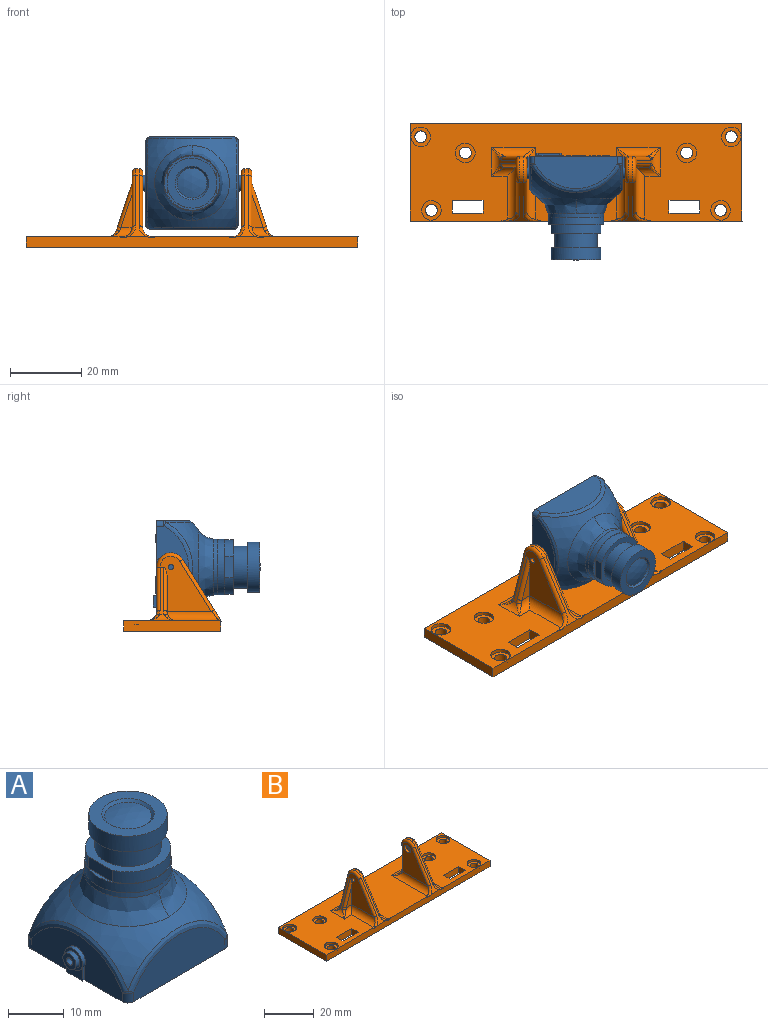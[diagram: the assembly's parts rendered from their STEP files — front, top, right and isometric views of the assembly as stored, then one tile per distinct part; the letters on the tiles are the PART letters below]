
ASSEMBLY  parts=2 mates=1
PART A: 309 faces, bbox 33.6x27.9x30.4 mm
  f0: sphere r=14.51mm, area 0mm2, adj f1
  f1: cone r=4.2mm half-angle=44deg, axis (0,0,1), area 19.4mm2, adj f0,f2
  f2: plane 14.21x14.21mm, normal (0,0,1), area 84.8mm2, adj f1,f3
  f3: cylinder r=7mm len=14mm, axis (0,0,-1), area 149.5mm2, adj f2,f4
  f4: plane 14.17x14.17mm, normal (0,0,-1), area 44.8mm2, adj f3,f5
  f5: cylinder r=5.9mm len=11.8mm, axis (0,0,-1), area 148.3mm2, adj f4,f6
  f6: plane 15.49x14.29mm, normal (0,0,1), area 67.2mm2, adj f5,f8,f9,f10,f11
  f7: plane 1.52x1.52mm, normal (-1,0,0), area 1.8mm2, adj f14
  f8: plane 5.92x2.5mm, normal (1,0,0), area 14.8mm2, adj f6,f9,f11,f13
  f9: cylinder r=7.6mm len=14mm, axis (0,0,1), area 44.5mm2, adj f6,f8,f10,f13
  f10: plane 5.92x2.5mm, normal (-1,0,0), area 14.8mm2, adj f6,f9,f11,f13
  f11: cylinder r=7.6mm len=14mm, axis (0,0,1), area 44.5mm2, adj f6,f8,f10,f13
  f12: plane 1.52x1.52mm, normal (1,0,0), area 1.8mm2, adj f16
  f13: plane 15.73x15.73mm, normal (0,0,1), area 11.8mm2, adj f8,f9,f10,f11,f15
  f14: cylinder r=0.75mm len=1.8mm, axis (1,0,0), area 8.5mm2, adj f7,f17
  f15: cylinder r=7.75mm len=15.5mm, axis (0,0,-1), area 97.4mm2, adj f13,f18
  f16: cylinder r=0.75mm len=1.8mm, axis (-1,0,0), area 8.5mm2, adj f12,f19
  f17: plane 3.35x3.35mm, normal (-1,0,0), area 6.8mm2, adj f14,f20
  f18: cone r=7.75mm half-angle=5.4deg, axis (0,0,-1), area 47.3mm2, adj f15,f21,f22
  f19: plane 3.35x3.35mm, normal (1,0,0), area 6.8mm2, adj f16,f23
  f20: cylinder r=1.65mm len=3.3mm, axis (1,0,0), area 10.4mm2, adj f17,f30
  f21: bspline ~20.97x10.73mm, area 147.9mm2, adj f18,f22,f31
  f22: bspline ~20.97x10.73mm, area 147.9mm2, adj f18,f21,f31
  f23: cylinder r=1.65mm len=3.3mm, axis (-1,0,0), area 10.4mm2, adj f19,f32
  f24: plane 0.96x0.69mm, normal (0,0,-1), area 0.3mm2, adj f33,f34,f35,f36,f37
  f25: plane 1.01x0.76mm, normal (0,0,-1), area 0.6mm2, adj f38,f39,f40
  f26: plane 0.99x0.91mm, normal (0,0,-1), area 0.7mm2, adj f41
  f27: plane 0.96x0.77mm, normal (0,0,-1), area 0.6mm2, adj f42,f43,f44,f45
  f28: plane 0.96x0.77mm, normal (0,0,-1), area 0.6mm2, adj f46,f47,f48,f49
  f29: plane 0.96x0.77mm, normal (0,0,-1), area 0.6mm2, adj f50,f51,f52,f53
  f30: plane 4.56x4.56mm, normal (-1,0,0), area 7.3mm2, adj f20,f61
  f31: sphere r=18.88mm, area 390.1mm2, adj f21,f22,f55,f59,f63,f67
  f32: plane 4.56x4.56mm, normal (1,0,0), area 7.3mm2, adj f23,f69
  f33: plane 0.58x0.25mm, normal (0.94,0.35,0), area 0.2mm2, adj f24,f34,f37,f75
  f34: bspline ~0.38x0.25mm, area 0.1mm2, adj f24,f33,f35,f75
  f35: bspline ~0.42x0.25mm, area 0.1mm2, adj f24,f34,f36,f75
  f36: plane 0.55x0.25mm, normal (-0.93,0.36,0), area 0.1mm2, adj f24,f35,f37,f75
  f37: plane 0.69x0.25mm, normal (0,-1,0), area 0.2mm2, adj f24,f33,f36,f75
  f38: plane 0.71x0.25mm, normal (1,0,0), area 0.2mm2, adj f25,f39,f40,f78
  f39: bspline ~0.73x0.25mm, area 0.2mm2, adj f25,f38,f40,f78
  f40: bspline ~0.95x0.69mm, area 0.4mm2, adj f25,f38,f39,f78
  f41: bspline ~0.95x0.89mm, area 0.7mm2, adj f26,f84
  f42: plane 0.9x0.25mm, normal (0,-1,0), area 0.2mm2, adj f27,f43,f44,f86
  f43: bspline ~0.49x0.25mm, area 0.1mm2, adj f27,f42,f45,f86
  f44: bspline ~0.59x0.25mm, area 0.2mm2, adj f27,f42,f45,f86
  f45: bspline ~0.8x0.25mm, area 0.2mm2, adj f27,f43,f44,f86
  f46: plane 0.9x0.25mm, normal (0,-1,0), area 0.2mm2, adj f28,f47,f48,f89
  f47: bspline ~0.49x0.25mm, area 0.1mm2, adj f28,f46,f49,f89
  f48: bspline ~0.59x0.25mm, area 0.2mm2, adj f28,f46,f49,f89
  f49: bspline ~0.8x0.25mm, area 0.2mm2, adj f28,f47,f48,f89
  f50: plane 0.9x0.25mm, normal (0,-1,0), area 0.2mm2, adj f29,f51,f52,f92
  f51: bspline ~0.49x0.25mm, area 0.1mm2, adj f29,f50,f53,f92
  f52: bspline ~0.59x0.25mm, area 0.2mm2, adj f29,f50,f53,f92
  f53: bspline ~0.8x0.25mm, area 0.2mm2, adj f29,f51,f52,f92
  f54: sphere r=1.5mm, area 0.6mm2, adj f55,f67,f98
  f55: bspline ~27.34x11.13mm, area 37.5mm2, adj f31,f54,f56,f99
  f56: sphere r=1.5mm, area 0.6mm2, adj f55,f59,f100
  f57: plane 4.09x3.01mm, normal (-1,0,0), area 8.2mm2, adj f58,f60,f61,f101
  f58: plane 2.92x0.5mm, normal (0,-1,0), area 1.5mm2, adj f57,f61,f101,f102
  f59: bspline ~27.64x11.52mm, area 37.5mm2, adj f31,f56,f62,f102
  f60: plane 2.92x0.5mm, normal (0,1,0), area 1.5mm2, adj f57,f61,f101,f102
  f61: cylinder r=2.25mm len=4.5mm, axis (1,0,0), area 8.8mm2, adj f30,f57,f58,f60,f102
  f62: sphere r=1.5mm, area 0.6mm2, adj f59,f63,f103
  f63: bspline ~27.34x11.12mm, area 37.5mm2, adj f31,f62,f64,f104
  f64: sphere r=1.5mm, area 0.6mm2, adj f63,f67,f105
  f65: plane 4.09x3.01mm, normal (1,0,0), area 8.2mm2, adj f66,f68,f69,f106
  f66: plane 2.92x0.5mm, normal (0,1,0), area 1.5mm2, adj f65,f69,f106,f107
  f67: bspline ~27.64x11.52mm, area 37.5mm2, adj f31,f54,f64,f107
  f68: plane 2.92x0.5mm, normal (0,-1,0), area 1.5mm2, adj f65,f69,f106,f107
  f69: cylinder r=2.25mm len=4.5mm, axis (-1,0,0), area 8.8mm2, adj f32,f65,f66,f68,f107
  f70: plane 6x2.95mm, normal (0,0,-1), area 17.7mm2, adj f108,f302,f303,f304
  f71: plane 5.78x1.83mm, normal (0,0,-1), area 9.7mm2, adj f109,f110,f111,f112
  f72: plane 5.78x1.83mm, normal (0,0,-1), area 9.7mm2, adj f113,f114,f115,f116
  f73: plane 5.78x1.83mm, normal (0,0,-1), area 9.7mm2, adj f117,f118,f119,f120
  f74: plane 2.04x1.97mm, normal (0,0,-1), area 1.9mm2, adj f121,f122,f123,f124,f125,f126,f127,f128
  f75: plane 1.99x1.84mm, normal (0,0,-1), area 1.2mm2, adj f33,f34,f35,f36,f37,f136,f137,f138
  f76: plane 2.09x1.78mm, normal (0,0,-1), area 1.2mm2, adj f144,f145,f146,f147
  f77: plane 1.99x1.84mm, normal (0,0,-1), area 1mm2, adj f148,f149,f150,f151,f152,f153,f154,f155
  f78: plane 2.04x1.53mm, normal (0,0,-1), area 1.2mm2, adj f38,f39,f40,f157,f158,f159,f160,f161
  f79: plane 1.99x1.34mm, normal (0,0,-1), area 1mm2, adj f162,f163,f164,f165,f166,f167,f168,f169
  f80: plane 1.99x0.27mm, normal (0,0,-1), area 0.5mm2, adj f172,f173,f174,f175
  f81: plane 1.99x1.54mm, normal (0,0,-1), area 1.5mm2, adj f176,f177,f178,f179,f180,f181,f182,f183
  f82: plane 1.99x0.27mm, normal (0,0,-1), area 0.5mm2, adj f186,f187,f188,f189
  f83: plane 2.04x1.97mm, normal (0,0,-1), area 1.9mm2, adj f190,f191,f192,f193,f194,f195,f196,f197
  f84: plane 1.26x1.26mm, normal (0,0,-1), area 0.5mm2, adj f41,f205
  f85: plane 1.22x1.02mm, normal (0,0,-1), area 0.5mm2, adj f206,f207,f208,f209,f210,f211,f212,f213
  f86: plane 1.22x1.11mm, normal (0,0,-1), area 0.5mm2, adj f42,f43,f44,f45,f214,f215,f216,f217
  f87: plane 1.2x1.17mm, normal (0,0,-1), area 0.4mm2, adj f218,f219,f220,f221,f222,f223,f224,f225
  f88: plane 1.17x0.17mm, normal (0,0,-1), area 0.2mm2, adj f227,f228,f229,f230
  f89: plane 1.22x1.11mm, normal (0,0,-1), area 0.5mm2, adj f46,f47,f48,f49,f231,f232,f233,f234
  f90: plane 1.26x1.25mm, normal (0,0,-1), area 0.6mm2, adj f235,f236,f237,f238,f239,f240,f241,f242
  f91: plane 1.17x1mm, normal (0,0,-1), area 0.6mm2, adj f244,f245,f246,f247,f248,f249,f250,f251
  f92: plane 1.22x1.11mm, normal (0,0,-1), area 0.5mm2, adj f50,f51,f52,f53,f254,f255,f256,f257
  f93: plane 1.2x0.86mm, normal (0,0,-1), area 0.4mm2, adj f258,f259,f260,f261,f262,f263,f264,f265
  f94: plane 0.49x0.14mm, normal (0,0,-1), area 0.1mm2, adj f268,f269,f270,f271
  f95: plane 1.22x0.89mm, normal (0,0,-1), area 0.4mm2, adj f272,f273,f274,f275,f276,f277,f278,f279
  f96: plane 1.22x0.89mm, normal (0,0,-1), area 0.4mm2, adj f281,f282,f283,f284,f285,f286,f287,f288
  f97: plane 1.2x1.17mm, normal (0,0,-1), area 0.4mm2, adj f290,f291,f292,f293,f294,f295,f296,f297
  f98: cylinder r=1.5mm len=2.04mm, axis (0,0,1), area 4.8mm2, adj f54,f99,f107,f305
  f99: plane 23x8.94mm, normal (0,-1,0), area 160mm2, adj f55,f98,f100,f305
  f100: cylinder r=1.5mm len=2.04mm, axis (0,0,-1), area 4.8mm2, adj f56,f99,f102,f305
  f101: plane 4x0.5mm, normal (0,0,-1), area 2mm2, adj f57,f58,f60,f305
  f102: plane 23.01x8.95mm, normal (-1,0,0), area 135.9mm2, adj f58,f59,f60,f61,f100,f103,f305
  f103: cylinder r=1.5mm len=2.04mm, axis (0,0,-1), area 4.8mm2, adj f62,f102,f104,f305
  f104: plane 23x8.94mm, normal (0,1,0), area 160mm2, adj f63,f103,f105,f305
  f105: cylinder r=1.5mm len=2.04mm, axis (0,0,-1), area 4.8mm2, adj f64,f104,f107,f305
  f106: plane 4x0.5mm, normal (0,0,-1), area 2mm2, adj f65,f66,f68,f305
  f107: plane 23.01x8.95mm, normal (1,0,0), area 135.9mm2, adj f66,f67,f68,f69,f98,f105,f305
  f108: plane 6x2mm, normal (0,1,0), area 12mm2, adj f70,f302,f304,f305
  f109: cylinder r=0.9mm len=2mm, axis (0,0,1), area 5.7mm2, adj f71,f110,f112,f305
  f110: plane 3.95x2mm, normal (0,-1,0), area 7.9mm2, adj f71,f109,f111,f305
  f111: cylinder r=0.9mm len=2mm, axis (0,0,1), area 5.7mm2, adj f71,f110,f112,f305
  f112: plane 3.95x2mm, normal (0,1,0), area 7.9mm2, adj f71,f109,f111,f305
  f113: cylinder r=0.9mm len=2mm, axis (0,0,1), area 5.7mm2, adj f72,f114,f116,f305
  f114: plane 3.95x2mm, normal (0,-1,0), area 7.9mm2, adj f72,f113,f115,f305
  f115: cylinder r=0.9mm len=2mm, axis (0,0,1), area 5.7mm2, adj f72,f114,f116,f305
  f116: plane 3.95x2mm, normal (0,1,0), area 7.9mm2, adj f72,f113,f115,f305
  f117: cylinder r=0.9mm len=2mm, axis (0,0,1), area 5.7mm2, adj f73,f118,f120,f305
  f118: plane 3.95x2mm, normal (0,-1,0), area 7.9mm2, adj f73,f117,f119,f305
  f119: cylinder r=0.9mm len=2mm, axis (0,0,1), area 5.7mm2, adj f73,f118,f120,f305
  f120: plane 3.95x2mm, normal (0,1,0), area 7.9mm2, adj f73,f117,f119,f305
  f121: plane 1.99x0.25mm, normal (-1,0,0), area 0.5mm2, adj f74,f122,f135,f305
  f122: plane 0.4x0.25mm, normal (0,-1,0), area 0.1mm2, adj f74,f121,f124,f305
  f123: bspline ~0.29x0.25mm, area 0.1mm2, adj f74,f124,f126,f305
  f124: plane 1.4x0.47mm, normal (0.95,-0.32,0), area 0.4mm2, adj f74,f122,f123,f305
  f125: plane 1.38x0.49mm, normal (-0.94,-0.34,0), area 0.4mm2, adj f74,f126,f127,f305
  f126: bspline ~0.32x0.25mm, area 0.1mm2, adj f74,f123,f125,f305
  f127: plane 0.35x0.25mm, normal (0,-1,0), area 0.1mm2, adj f74,f125,f128,f305
  f128: plane 1.99x0.25mm, normal (1,0,0), area 0.5mm2, adj f74,f127,f129,f305
  f129: plane 0.27x0.25mm, normal (0,1,0), area 0.1mm2, adj f74,f128,f130,f305
  f130: plane 1.66x0.25mm, normal (-1,0,0), area 0.4mm2, adj f74,f129,f131,f305
  f131: plane 1.66x0.59mm, normal (0.94,0.33,0), area 0.4mm2, adj f74,f130,f132,f305
  f132: plane 0.25x0.23mm, normal (0,1,0), area 0.1mm2, adj f74,f131,f133,f305
  f133: plane 1.69x0.57mm, normal (-0.95,0.32,0), area 0.4mm2, adj f74,f132,f134,f305
  f134: plane 1.69x0.25mm, normal (1,0,0), area 0.4mm2, adj f74,f133,f135,f305
  f135: plane 0.27x0.25mm, normal (0,1,0), area 0.1mm2, adj f74,f121,f134,f305
  f136: plane 1.99x0.76mm, normal (-0.93,-0.36,0), area 0.5mm2, adj f75,f137,f143,f305
  f137: plane 0.29x0.25mm, normal (0,-1,0), area 0.1mm2, adj f75,f136,f138,f305
  f138: plane 1.99x0.8mm, normal (0.93,-0.37,0), area 0.5mm2, adj f75,f137,f139,f305
  f139: plane 0.28x0.25mm, normal (0,1,0), area 0.1mm2, adj f75,f138,f140,f305
  f140: plane 0.6x0.25mm, normal (-0.94,0.35,0), area 0.2mm2, adj f75,f139,f141,f305
  f141: plane 0.85x0.25mm, normal (0,1,0), area 0.2mm2, adj f75,f140,f142,f305
  f142: plane 0.6x0.25mm, normal (0.94,0.33,0), area 0.2mm2, adj f75,f141,f143,f305
  f143: plane 0.28x0.25mm, normal (0,1,0), area 0.1mm2, adj f75,f136,f142,f305
  f144: plane 0.27x0.25mm, normal (0.24,-0.97,0), area 0.1mm2, adj f76,f145,f147,f305
  f145: bspline ~2.06x1.76mm, area 1.3mm2, adj f76,f144,f146,f305
  f146: plane 0.27x0.25mm, normal (0.22,0.97,0), area 0.1mm2, adj f76,f145,f147,f305
  f147: bspline ~1.6x1.23mm, area 1mm2, adj f76,f144,f146,f305
  f148: plane 1.99x0.76mm, normal (-0.93,0.36,0), area 0.5mm2, adj f77,f149,f156,f305
  f149: plane 0.28x0.25mm, normal (0,-1,0), area 0.1mm2, adj f77,f148,f151,f305
  f150: bspline ~0.32x0.25mm, area 0.1mm2, adj f77,f151,f153,f305
  f151: plane 1.44x0.52mm, normal (0.94,-0.34,0), area 0.4mm2, adj f77,f149,f150,f305
  f152: plane 1.44x0.55mm, normal (-0.93,-0.36,0), area 0.4mm2, adj f77,f153,f154,f305
  f153: bspline ~0.32x0.25mm, area 0.1mm2, adj f77,f150,f152,f305
  f154: plane 0.28x0.25mm, normal (0,-1,0), area 0.1mm2, adj f77,f152,f155,f305
  f155: plane 1.99x0.79mm, normal (0.93,0.37,0), area 0.5mm2, adj f77,f154,f156,f305
  f156: plane 0.29x0.25mm, normal (0,1,0), area 0.1mm2, adj f77,f148,f155,f305
  f157: plane 1.99x0.25mm, normal (-1,0,0), area 0.5mm2, adj f78,f159,f161,f305
  f158: bspline ~1.22x1.15mm, area 0.6mm2, adj f78,f159,f160,f305
  f159: bspline ~1.03x0.25mm, area 0.3mm2, adj f78,f157,f158,f305
  f160: plane 0.82x0.25mm, normal (1,0,0), area 0.2mm2, adj f78,f158,f161,f305
  f161: plane 0.27x0.25mm, normal (0,1,0), area 0.1mm2, adj f78,f157,f160,f305
  f162: plane 1.99x0.25mm, normal (-1,0,0), area 0.5mm2, adj f79,f163,f171,f305
  f163: plane 1.34x0.25mm, normal (0,-1,0), area 0.3mm2, adj f79,f162,f164,f305
  f164: plane 0.25x0.23mm, normal (1,0,0), area 0.1mm2, adj f79,f163,f165,f305
  f165: plane 1.07x0.25mm, normal (0,1,0), area 0.3mm2, adj f79,f164,f166,f305
  f166: plane 0.63x0.25mm, normal (1,0,0), area 0.2mm2, adj f79,f165,f167,f305
  f167: plane 0.93x0.25mm, normal (0,-1,0), area 0.2mm2, adj f79,f166,f168,f305
  f168: plane 0.25x0.23mm, normal (1,0,0), area 0.1mm2, adj f79,f167,f169,f305
  f169: plane 0.93x0.25mm, normal (0,1,0), area 0.2mm2, adj f79,f168,f170,f305
  f170: plane 0.9x0.25mm, normal (1,0,0), area 0.2mm2, adj f79,f169,f171,f305
  f171: plane 0.27x0.25mm, normal (0,1,0), area 0.1mm2, adj f79,f162,f170,f305
  f172: plane 1.99x0.25mm, normal (-1,0,0), area 0.5mm2, adj f80,f173,f175,f305
  f173: plane 0.27x0.25mm, normal (0,-1,0), area 0.1mm2, adj f80,f172,f174,f305
  f174: plane 1.99x0.25mm, normal (1,0,0), area 0.5mm2, adj f80,f173,f175,f305
  f175: plane 0.27x0.25mm, normal (0,1,0), area 0.1mm2, adj f80,f172,f174,f305
  f176: plane 1.99x0.25mm, normal (-1,0,0), area 0.5mm2, adj f81,f177,f185,f305
  f177: plane 0.28x0.25mm, normal (0,-1,0), area 0.1mm2, adj f81,f176,f178,f305
  f178: plane 1.52x1mm, normal (0.84,-0.55,0), area 0.5mm2, adj f81,f177,f179,f305
  f179: plane 1.52x0.25mm, normal (-1,0,0), area 0.4mm2, adj f81,f178,f180,f305
  f180: plane 0.27x0.25mm, normal (0,-1,0), area 0.1mm2, adj f81,f179,f181,f305
  f181: plane 1.99x0.25mm, normal (1,0,0), area 0.5mm2, adj f81,f180,f182,f305
  f182: plane 0.28x0.25mm, normal (0,1,0), area 0.1mm2, adj f81,f181,f183,f305
  f183: plane 1.52x1mm, normal (-0.84,0.55,0), area 0.5mm2, adj f81,f182,f184,f305
  f184: plane 1.52x0.25mm, normal (1,0,0), area 0.4mm2, adj f81,f183,f185,f305
  f185: plane 0.27x0.25mm, normal (0,1,0), area 0.1mm2, adj f81,f176,f184,f305
  f186: plane 1.99x0.25mm, normal (-1,0,0), area 0.5mm2, adj f82,f187,f189,f305
  f187: plane 0.27x0.25mm, normal (0,-1,0), area 0.1mm2, adj f82,f186,f188,f305
  f188: plane 1.99x0.25mm, normal (1,0,0), area 0.5mm2, adj f82,f187,f189,f305
  f189: plane 0.27x0.25mm, normal (0,1,0), area 0.1mm2, adj f82,f186,f188,f305
  f190: plane 1.99x0.25mm, normal (-1,0,0), area 0.5mm2, adj f83,f191,f204,f305
  f191: plane 0.4x0.25mm, normal (0,-1,0), area 0.1mm2, adj f83,f190,f193,f305
  f192: bspline ~0.29x0.25mm, area 0.1mm2, adj f83,f193,f195,f305
  f193: plane 1.4x0.47mm, normal (0.95,-0.32,0), area 0.4mm2, adj f83,f191,f192,f305
  f194: plane 1.38x0.49mm, normal (-0.94,-0.34,0), area 0.4mm2, adj f83,f195,f196,f305
  f195: bspline ~0.32x0.25mm, area 0.1mm2, adj f83,f192,f194,f305
  f196: plane 0.35x0.25mm, normal (0,-1,0), area 0.1mm2, adj f83,f194,f197,f305
  f197: plane 1.99x0.25mm, normal (1,0,0), area 0.5mm2, adj f83,f196,f198,f305
  f198: plane 0.27x0.25mm, normal (0,1,0), area 0.1mm2, adj f83,f197,f199,f305
  f199: plane 1.66x0.25mm, normal (-1,0,0), area 0.4mm2, adj f83,f198,f200,f305
  f200: plane 1.66x0.59mm, normal (0.94,0.33,0), area 0.4mm2, adj f83,f199,f201,f305
  f201: plane 0.25x0.23mm, normal (0,1,0), area 0.1mm2, adj f83,f200,f202,f305
  f202: plane 1.69x0.57mm, normal (-0.95,0.32,0), area 0.4mm2, adj f83,f201,f203,f305
  f203: plane 1.69x0.25mm, normal (1,0,0), area 0.4mm2, adj f83,f202,f204,f305
  f204: plane 0.27x0.25mm, normal (0,1,0), area 0.1mm2, adj f83,f190,f203,f305
  f205: bspline ~1.23x1.22mm, area 1mm2, adj f84,f305
  f206: plane 0.25x0.16mm, normal (-1,0.04,0), area 0mm2, adj f85,f208,f211,f305
  f207: bspline ~0.94x0.58mm, area 0.4mm2, adj f85,f209,f210,f305
  f208: bspline ~0.68x0.37mm, area 0.3mm2, adj f85,f206,f209,f305
  f209: bspline ~0.47x0.25mm, area 0.1mm2, adj f85,f207,f208,f305
  f210: plane 0.25x0.17mm, normal (1,-0.04,0), area 0mm2, adj f85,f207,f212,f305
  f211: bspline ~1.02x0.64mm, area 0.5mm2, adj f85,f206,f213,f305
  f212: bspline ~0.6x0.28mm, area 0.2mm2, adj f85,f210,f213,f305
  f213: bspline ~0.53x0.25mm, area 0.1mm2, adj f85,f211,f212,f305
  f214: plane 1.17x0.25mm, normal (0,1,0), area 0.3mm2, adj f86,f215,f216,f305
  f215: bspline ~1.07x1.07mm, area 0.5mm2, adj f86,f214,f217,f305
  f216: bspline ~0.67x0.25mm, area 0.2mm2, adj f86,f214,f217,f305
  f217: bspline ~0.25x0.19mm, area 0.1mm2, adj f86,f215,f216,f305
  f218: plane 1.17x0.5mm, normal (0.39,0.92,0), area 0.3mm2, adj f87,f219,f226,f305
  f219: plane 0.25x0.18mm, normal (-1,0,0), area 0mm2, adj f87,f218,f221,f305
  f220: bspline ~0.25x0.19mm, area 0.1mm2, adj f87,f221,f223,f305
  f221: plane 0.85x0.34mm, normal (-0.37,-0.93,0), area 0.2mm2, adj f87,f219,f220,f305
  f222: plane 0.85x0.36mm, normal (-0.39,0.92,0), area 0.2mm2, adj f87,f223,f224,f305
  f223: bspline ~0.25x0.19mm, area 0.1mm2, adj f87,f220,f222,f305
  f224: plane 0.25x0.18mm, normal (-1,0,0), area 0mm2, adj f87,f222,f225,f305
  f225: plane 1.17x0.52mm, normal (0.4,-0.92,0), area 0.3mm2, adj f87,f224,f226,f305
  f226: plane 0.25x0.19mm, normal (1,0,0), area 0mm2, adj f87,f218,f225,f305
  f227: plane 1.17x0.25mm, normal (0,1,0), area 0.3mm2, adj f88,f228,f230,f305
  f228: plane 0.25x0.17mm, normal (-1,0,0), area 0mm2, adj f88,f227,f229,f305
  f229: plane 1.17x0.25mm, normal (0,-1,0), area 0.3mm2, adj f88,f228,f230,f305
  f230: plane 0.25x0.17mm, normal (1,0,0), area 0mm2, adj f88,f227,f229,f305
  f231: plane 1.17x0.25mm, normal (0,1,0), area 0.3mm2, adj f89,f232,f233,f305
  f232: bspline ~1.07x1.07mm, area 0.5mm2, adj f89,f231,f234,f305
  f233: bspline ~0.67x0.25mm, area 0.2mm2, adj f89,f231,f234,f305
  f234: bspline ~0.25x0.19mm, area 0.1mm2, adj f89,f232,f233,f305
  f235: plane 0.25x0.14mm, normal (0,1,0), area 0mm2, adj f90,f236,f243,f305
  f236: plane 0.55x0.25mm, normal (-1,0,0), area 0.1mm2, adj f90,f235,f237,f305
  f237: plane 0.44x0.25mm, normal (0,-1,0), area 0.1mm2, adj f90,f236,f238,f305
  f238: bspline ~1.22x1.21mm, area 0.8mm2, adj f90,f237,f239,f305
  f239: plane 0.25x0.16mm, normal (0.97,-0.24,0), area 0mm2, adj f90,f238,f241,f305
  f240: bspline ~0.86x0.71mm, area 0.4mm2, adj f90,f241,f242,f305
  f241: bspline ~0.81x0.25mm, area 0.3mm2, adj f90,f239,f240,f305
  f242: plane 0.25x0.22mm, normal (0,1,0), area 0.1mm2, adj f90,f240,f243,f305
  f243: plane 0.38x0.25mm, normal (1,0,0), area 0.1mm2, adj f90,f235,f242,f305
  f244: plane 1.17x0.25mm, normal (0,1,0), area 0.3mm2, adj f91,f245,f253,f305
  f245: plane 0.25x0.18mm, normal (-1,0,0), area 0mm2, adj f91,f244,f246,f305
  f246: plane 0.9x0.65mm, normal (-0.58,-0.81,0), area 0.3mm2, adj f91,f245,f247,f305
  f247: plane 0.9x0.25mm, normal (0,1,0), area 0.2mm2, adj f91,f246,f248,f305
  f248: plane 0.25x0.17mm, normal (-1,0,0), area 0mm2, adj f91,f247,f249,f305
  f249: plane 1.17x0.25mm, normal (0,-1,0), area 0.3mm2, adj f91,f248,f250,f305
  f250: plane 0.25x0.18mm, normal (1,0,0), area 0mm2, adj f91,f249,f251,f305
  f251: plane 0.9x0.65mm, normal (0.58,0.81,0), area 0.3mm2, adj f91,f250,f252,f305
  f252: plane 0.9x0.25mm, normal (0,-1,0), area 0.2mm2, adj f91,f251,f253,f305
  f253: plane 0.25x0.17mm, normal (1,0,0), area 0mm2, adj f91,f244,f252,f305
  f254: plane 1.17x0.25mm, normal (0,1,0), area 0.3mm2, adj f92,f255,f256,f305
  f255: bspline ~1.07x1.07mm, area 0.5mm2, adj f92,f254,f257,f305
  f256: bspline ~0.67x0.25mm, area 0.2mm2, adj f92,f254,f257,f305
  f257: bspline ~0.25x0.19mm, area 0.1mm2, adj f92,f255,f256,f305
  f258: plane 0.25x0.16mm, normal (-1,0.09,0), area 0mm2, adj f93,f259,f266,f305
  f259: bspline ~0.56x0.53mm, area 0.4mm2, adj f93,f258,f260,f305
  f260: plane 0.25x0.15mm, normal (0.99,0.14,0), area 0mm2, adj f93,f259,f261,f305
  f261: plane 0.61x0.25mm, normal (-0.21,0.98,0), area 0.2mm2, adj f93,f260,f262,f305
  f262: plane 0.62x0.25mm, normal (-1,0,0), area 0.2mm2, adj f93,f261,f263,f305
  f263: plane 0.25x0.14mm, normal (0,-1,0), area 0mm2, adj f93,f262,f264,f305
  f264: plane 0.49x0.25mm, normal (1,0,0), area 0.1mm2, adj f93,f263,f265,f305
  f265: plane 0.31x0.25mm, normal (0.21,-0.98,0), area 0.1mm2, adj f93,f264,f267,f305
  f266: bspline ~0.75x0.33mm, area 0.2mm2, adj f93,f258,f267,f305
  f267: bspline ~0.66x0.63mm, area 0.3mm2, adj f93,f265,f266,f305
  f268: plane 0.25x0.14mm, normal (0,1,0), area 0mm2, adj f94,f269,f271,f305
  f269: plane 0.49x0.25mm, normal (-1,0,0), area 0.1mm2, adj f94,f268,f270,f305
  f270: plane 0.25x0.14mm, normal (0,-1,0), area 0mm2, adj f94,f269,f271,f305
  f271: plane 0.49x0.25mm, normal (1,0,0), area 0.1mm2, adj f94,f268,f270,f305
  f272: plane 0.25x0.14mm, normal (0,-1,0), area 0mm2, adj f95,f273,f280,f305
  f273: plane 0.85x0.25mm, normal (1,0,0), area 0.2mm2, adj f95,f272,f275,f305
  f274: bspline ~0.62x0.51mm, area 0.3mm2, adj f95,f276,f277,f305
  f275: bspline ~0.25x0.1mm, area 0mm2, adj f95,f273,f276,f305
  f276: bspline ~0.34x0.3mm, area 0.1mm2, adj f95,f274,f275,f305
  f277: plane 0.25x0.16mm, normal (0.99,0.14,0), area 0mm2, adj f95,f274,f279,f305
  f278: bspline ~0.26x0.25mm, area 0.1mm2, adj f95,f279,f280,f305
  f279: bspline ~0.82x0.81mm, area 0.5mm2, adj f95,f277,f278,f305
  f280: plane 0.64x0.25mm, normal (-1,0,0), area 0.2mm2, adj f95,f272,f278,f305
  f281: plane 0.25x0.14mm, normal (0,-1,0), area 0mm2, adj f96,f282,f289,f305
  f282: plane 0.85x0.25mm, normal (1,0,0), area 0.2mm2, adj f96,f281,f284,f305
  f283: bspline ~0.62x0.51mm, area 0.3mm2, adj f96,f285,f286,f305
  f284: bspline ~0.25x0.1mm, area 0mm2, adj f96,f282,f285,f305
  f285: bspline ~0.34x0.3mm, area 0.1mm2, adj f96,f283,f284,f305
  f286: plane 0.25x0.16mm, normal (0.99,0.14,0), area 0mm2, adj f96,f283,f288,f305
  f287: bspline ~0.26x0.25mm, area 0.1mm2, adj f96,f288,f289,f305
  f288: bspline ~0.82x0.81mm, area 0.5mm2, adj f96,f286,f287,f305
  f289: plane 0.64x0.25mm, normal (-1,0,0), area 0.2mm2, adj f96,f281,f287,f305
  f290: plane 1.17x0.5mm, normal (0.39,0.92,0), area 0.3mm2, adj f97,f291,f298,f305
  f291: plane 0.25x0.18mm, normal (-1,0,0), area 0mm2, adj f97,f290,f293,f305
  f292: bspline ~0.25x0.19mm, area 0.1mm2, adj f97,f293,f295,f305
  f293: plane 0.85x0.34mm, normal (-0.37,-0.93,0), area 0.2mm2, adj f97,f291,f292,f305
  f294: plane 0.85x0.36mm, normal (-0.39,0.92,0), area 0.2mm2, adj f97,f295,f296,f305
  f295: bspline ~0.25x0.19mm, area 0.1mm2, adj f97,f292,f294,f305
  f296: plane 0.25x0.18mm, normal (-1,0,0), area 0mm2, adj f97,f294,f297,f305
  f297: plane 1.17x0.52mm, normal (0.4,-0.92,0), area 0.3mm2, adj f97,f296,f298,f305
  f298: plane 0.25x0.19mm, normal (1,0,0), area 0mm2, adj f97,f290,f297,f305
  f299: plane 7x1mm, normal (0,1,0), area 7mm2, adj f300,f305,f306,f307
  f300: plane 3.2x1mm, normal (1,0,0), area 3.2mm2, adj f299,f301,f305,f307
  f301: plane 1x0.5mm, normal (0,-1,0), area 0.5mm2, adj f300,f302,f305,f307
  f302: plane 3x2.95mm, normal (-1,0,0), area 8.8mm2, adj f70,f108,f301,f303,f307
  f303: plane 6x3mm, normal (0,-1,0), area 18mm2, adj f70,f302,f304,f307
  f304: plane 3x2.95mm, normal (1,0,0), area 8.8mm2, adj f70,f108,f303,f307,f308
  f305: plane 26.05x26.05mm, normal (0,0,-1), area 601.4mm2, adj f98,f99,f100,f101,f102,f103,f104,f105
  f306: plane 3.2x1mm, normal (-1,0,0), area 3.2mm2, adj f299,f305,f307,f308
  f307: plane 7x3.2mm, normal (0,0,-1), area 4.7mm2, adj f299,f300,f301,f302,f303,f304,f306,f308
  f308: plane 1x0.5mm, normal (0,-1,0), area 0.5mm2, adj f304,f305,f306,f307
PART B: 90 faces, bbox 94.3x28.8x23.6 mm
  f0: plane 93.17x27.41mm, normal (0,0,1), area 1929.5mm2, adj f9,f10,f11,f12,f13,f14,f15,f16
  f1: plane 15.5x14.33mm, normal (-1,0,0), area 136.3mm2, adj f48,f52,f86,f87,f88
  f2: plane 16.76x15.59mm, normal (-1,0,0), area 118.8mm2, adj f37,f41,f42,f59,f72,f73,f77
  f3: cylinder r=1.65mm len=3.3mm, axis (0,0,-1), area 20.7mm2, adj f21,f33
  f4: cylinder r=1.65mm len=3.3mm, axis (0,0,-1), area 20.7mm2, adj f21,f31
  f5: cylinder r=1.65mm len=3.3mm, axis (0,0,-1), area 20.7mm2, adj f21,f27
  f6: cylinder r=1.65mm len=3.3mm, axis (0,0,-1), area 20.7mm2, adj f21,f23
  f7: cylinder r=1.65mm len=3.3mm, axis (0,0,-1), area 20.7mm2, adj f21,f29
  f8: cylinder r=1.65mm len=3.3mm, axis (0,0,-1), area 20.7mm2, adj f21,f25
  f9: plane 27.24x3mm, normal (-1,0,0), area 81.7mm2, adj f0,f10,f18,f21
  f10: plane 93.84x3.84mm, normal (0,-1,0), area 277.7mm2, adj f0,f9,f11,f21,f35,f45,f62,f71
  f11: plane 27.24x3mm, normal (1,0,0), area 81.7mm2, adj f0,f10,f18,f21
  f12: plane 3.6x3mm, normal (1,0,0), area 10.8mm2, adj f0,f13,f19,f21
  f13: plane 8.6x3mm, normal (0,-1,0), area 25.8mm2, adj f0,f12,f14,f21
  f14: plane 3.6x3mm, normal (-1,0,0), area 10.8mm2, adj f0,f13,f19,f21
  f15: plane 8.6x3mm, normal (0,-1,0), area 25.8mm2, adj f0,f16,f20,f21
  f16: plane 3.6x3mm, normal (-1,0,0), area 10.8mm2, adj f0,f15,f17,f21
  f17: plane 8.6x3mm, normal (0,1,0), area 25.8mm2, adj f0,f16,f20,f21
  f18: plane 93x3mm, normal (0,1,0), area 279mm2, adj f0,f9,f11,f21
  f19: plane 8.6x3mm, normal (0,1,0), area 25.8mm2, adj f0,f12,f14,f21
  f20: plane 3.6x3mm, normal (1,0,0), area 10.8mm2, adj f0,f15,f17,f21
  f21: plane 93x27.24mm, normal (0,0,-1), area 2419.9mm2, adj f3,f4,f5,f6,f7,f8,f9,f10
  f22: cylinder r=2.75mm len=5.5mm, axis (0,0,1), area 17.3mm2, adj f0,f23
  f23: plane 5.5x5.5mm, normal (0,0,1), area 15.2mm2, adj f6,f22
  f24: cylinder r=2.75mm len=5.5mm, axis (0,0,1), area 17.3mm2, adj f0,f25
  f25: plane 5.5x5.5mm, normal (0,0,1), area 15.2mm2, adj f8,f24
  f26: cylinder r=2.75mm len=5.5mm, axis (0,0,1), area 17.3mm2, adj f0,f27
  f27: plane 5.5x5.5mm, normal (0,0,1), area 15.2mm2, adj f5,f26
  f28: cylinder r=2.75mm len=5.5mm, axis (0,0,1), area 17.3mm2, adj f0,f29
  f29: plane 5.5x5.5mm, normal (0,0,1), area 15.2mm2, adj f7,f28
  f30: cylinder r=2.75mm len=5.5mm, axis (0,0,1), area 17.3mm2, adj f0,f31
  f31: plane 5.5x5.5mm, normal (0,0,1), area 15.2mm2, adj f4,f30
  f32: cylinder r=2.75mm len=5.5mm, axis (0,0,1), area 17.3mm2, adj f0,f33
  f33: plane 5.5x5.5mm, normal (0,0,1), area 15.2mm2, adj f3,f32
  f34: cylinder r=4mm len=7.39mm, axis (1,0,0), area 10.3mm2, adj f35,f36,f73,f74,f82
  f35: plane 17.12x10.67mm, normal (0,-0.85,0.53), area 23.8mm2, adj f10,f34,f71,f72,f80,f81
  f36: plane 12.5x5.11mm, normal (0,1,0), area 37.8mm2, adj f34,f58,f74,f83
  f37: cylinder r=0.75mm len=2mm, axis (1,0,0), area 9.4mm2, adj f2,f40
  f38: plane 15.5x14.33mm, normal (1,0,0), area 136.3mm2, adj f39,f57,f81,f82,f83
  f39: cylinder r=1.65mm len=3.3mm, axis (1,0,0), area 10.4mm2, adj f38,f40
  f40: plane 3.3x3.3mm, normal (1,0,0), area 6.8mm2, adj f37,f39
  f41: plane 13.29x4.43mm, normal (-0.95,0,0.32), area 14.1mm2, adj f2,f60,f74,f75,f77,f78
  f42: plane 9.33x3.11mm, normal (0,-1,0), area 14.5mm2, adj f2,f61,f77
  f43: cylinder r=4mm len=7.39mm, axis (-1,0,0), area 10.3mm2, adj f44,f45,f64,f65,f87
  f44: plane 12.5x5.11mm, normal (0,1,0), area 37.8mm2, adj f43,f53,f65,f88
  f45: plane 17.12x10.67mm, normal (0,-0.85,0.53), area 23.8mm2, adj f10,f43,f62,f63,f85,f86
  f46: cylinder r=0.75mm len=2mm, axis (-1,0,0), area 9.4mm2, adj f47,f49
  f47: plane 16.76x15.59mm, normal (1,0,0), area 118.8mm2, adj f46,f50,f51,f55,f63,f64,f68
  f48: cylinder r=1.65mm len=3.3mm, axis (-1,0,0), area 10.4mm2, adj f1,f49
  f49: plane 3.3x3.3mm, normal (-1,0,0), area 6.8mm2, adj f46,f48
  f50: plane 13.29x4.43mm, normal (0.95,0,0.32), area 14.1mm2, adj f47,f54,f65,f66,f68,f69
  f51: plane 9.33x3.11mm, normal (0,-1,0), area 14.5mm2, adj f47,f56,f68
  f52: cylinder r=2.5mm len=20.01mm, axis (0,-1,0), area 67.4mm2, adj f0,f1,f85,f89
  f53: cylinder r=2.5mm len=12.3mm, axis (-1,0,0), area 31.5mm2, adj f0,f44,f66,f67,f89
  f54: cylinder r=2.5mm len=8mm, axis (0,-1,0), area 14.6mm2, adj f0,f50,f67,f70
  f55: cylinder r=2.5mm len=14.51mm, axis (0,1,0), area 47.8mm2, adj f0,f47,f56,f62
  f56: cylinder r=2.5mm len=6.8mm, axis (-1,0,0), area 15.1mm2, adj f0,f51,f55,f69,f70
  f57: cylinder r=2.5mm len=20.01mm, axis (0,-1,0), area 67.4mm2, adj f0,f38,f80,f84
  f58: cylinder r=2.5mm len=12.3mm, axis (-1,0,0), area 31.5mm2, adj f0,f36,f75,f76,f84
  f59: cylinder r=2.5mm len=14.51mm, axis (0,1,0), area 47.8mm2, adj f0,f2,f61,f71
  f60: cylinder r=2.5mm len=8mm, axis (0,1,0), area 14.6mm2, adj f0,f41,f76,f79
  f61: cylinder r=2.5mm len=6.8mm, axis (-1,0,0), area 15.1mm2, adj f0,f42,f59,f78,f79
  f62: bspline ~5.25x3.5mm, area 7.2mm2, adj f0,f10,f45,f55,f63
  f63: cylinder r=1mm len=14.62mm, axis (0,-0.53,-0.85), area 26.1mm2, adj f45,f47,f62,f64
  f64: torus R=3mm, axis (-1,0,0), area 14.8mm2, adj f43,f47,f63,f65
  f65: cylinder r=1mm len=12.82mm, axis (-0.32,0,0.95), area 20.3mm2, adj f43,f44,f50,f64,f66
  f66: bspline ~2.09x1.64mm, area 1.5mm2, adj f50,f53,f65,f67
  f67: bspline ~3.38x3.38mm, area 2.1mm2, adj f53,f54,f66
  f68: cylinder r=1mm len=12.5mm, axis (-0.32,0,0.95), area 17.8mm2, adj f47,f50,f51,f69
  f69: bspline ~2.09x1.64mm, area 1.5mm2, adj f50,f56,f68,f70
  f70: bspline ~3.38x3.38mm, area 2.1mm2, adj f54,f56,f69
  f71: bspline ~5.25x3.5mm, area 7.2mm2, adj f0,f10,f35,f59,f72
  f72: cylinder r=1mm len=14.62mm, axis (0,0.53,0.85), area 26.1mm2, adj f2,f35,f71,f73
  f73: torus R=3mm, axis (1,0,0), area 14.8mm2, adj f2,f34,f72,f74
  f74: cylinder r=1mm len=12.82mm, axis (0.32,0,0.95), area 20.3mm2, adj f34,f36,f41,f73,f75
  f75: bspline ~1.32x1.13mm, area 1.5mm2, adj f41,f58,f74,f76
  f76: bspline ~3.38x3.38mm, area 2.1mm2, adj f58,f60,f75
  f77: cylinder r=1mm len=12.5mm, axis (-0.32,0,-0.95), area 17.8mm2, adj f2,f41,f42,f78
  f78: bspline ~1.32x1.13mm, area 1.5mm2, adj f41,f61,f77,f79
  f79: bspline ~3.38x3.38mm, area 2.1mm2, adj f60,f61,f78
  f80: bspline ~5.25x3.5mm, area 7.2mm2, adj f0,f10,f35,f57,f81
  f81: cylinder r=1mm len=14.62mm, axis (0,-0.53,-0.85), area 26.1mm2, adj f35,f38,f80,f82
  f82: torus R=3mm, axis (1,0,0), area 14.8mm2, adj f34,f38,f81,f83
  f83: cylinder r=1mm len=12.5mm, axis (0,0,1), area 19.6mm2, adj f36,f38,f82,f84
  f84: bspline ~3.5x3.5mm, area 2.7mm2, adj f57,f58,f83
  f85: bspline ~5.25x3.5mm, area 7.2mm2, adj f0,f10,f45,f52,f86
  f86: cylinder r=1mm len=14.62mm, axis (0,0.53,0.85), area 26.1mm2, adj f1,f45,f85,f87
  f87: torus R=3mm, axis (-1,0,0), area 14.8mm2, adj f1,f43,f86,f88
  f88: cylinder r=1mm len=12.5mm, axis (0,0,-1), area 19.6mm2, adj f1,f44,f87,f89
  f89: bspline ~3.5x3.5mm, area 4.5mm2, adj f52,f53,f88
PLACE A rot(axis=(0,-0.71,0.71),180deg) t=(-8.34,13.12,47.42)mm
PLACE B rot(axis=(-0.46,0.75,0.48),0deg) t=(-8.34,9.69,9.12)mm
MATE revolute A.f23 <-> B.f34  axis (-1,0,0) through (-23.14,9.17,47.42)mm
